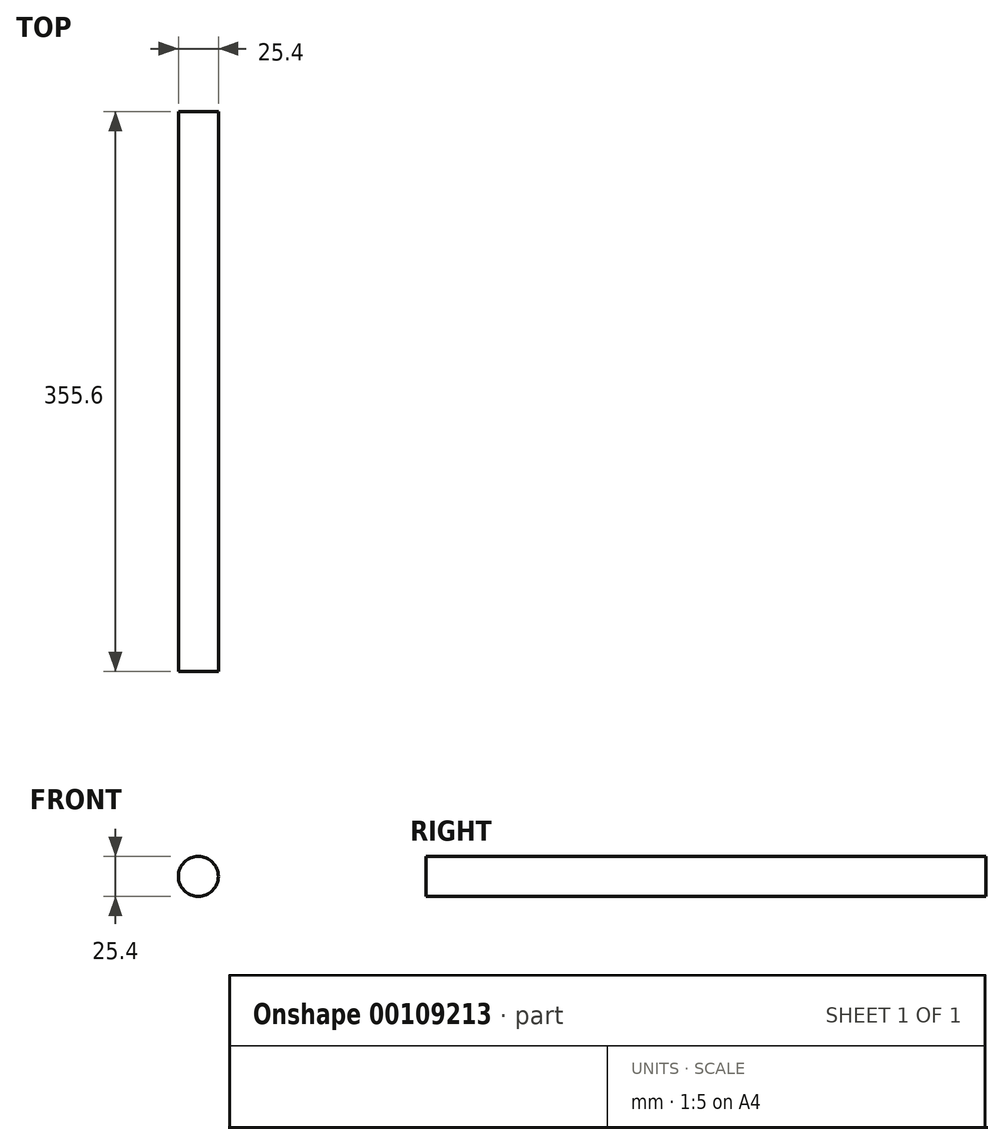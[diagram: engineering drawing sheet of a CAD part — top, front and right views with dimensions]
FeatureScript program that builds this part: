
annotation { "Feature Type Name" : "Feature", "Feature Type Description" : "" }
export const myFeature = defineFeature(function(context is Context, id is Id, definition is map)
    precondition{}
    {
        {
            var Q0;
            Q0=qCreatedBy(makeId("Front.planeOp"),FACE);
            var sketch = newSketch(context, id + "F0", { "sketchPlane" : qUnion([Q0])});
            skCircle(sketch, "E0", {"center": v(0, 0) * mm, "radius": 12.7 * mm});
            skSolve(sketch);
        }
        {
            var Q0;
            Q0=makeQuery(id+"F0.imprint","IMPRINT",FACE,{"disambiguationData":[TD([[makeQuery(id+"F0.imprint","IMPRINT",EDGE,{"derivedFrom":sQuery(id+"F0.wireOp",EDGE,"E0")}),1.0]])]});
            extrude(context, id + "F1", {"entities" : qUnion([Q0]), "depth" : 355.6 * mm});
        }
    });
